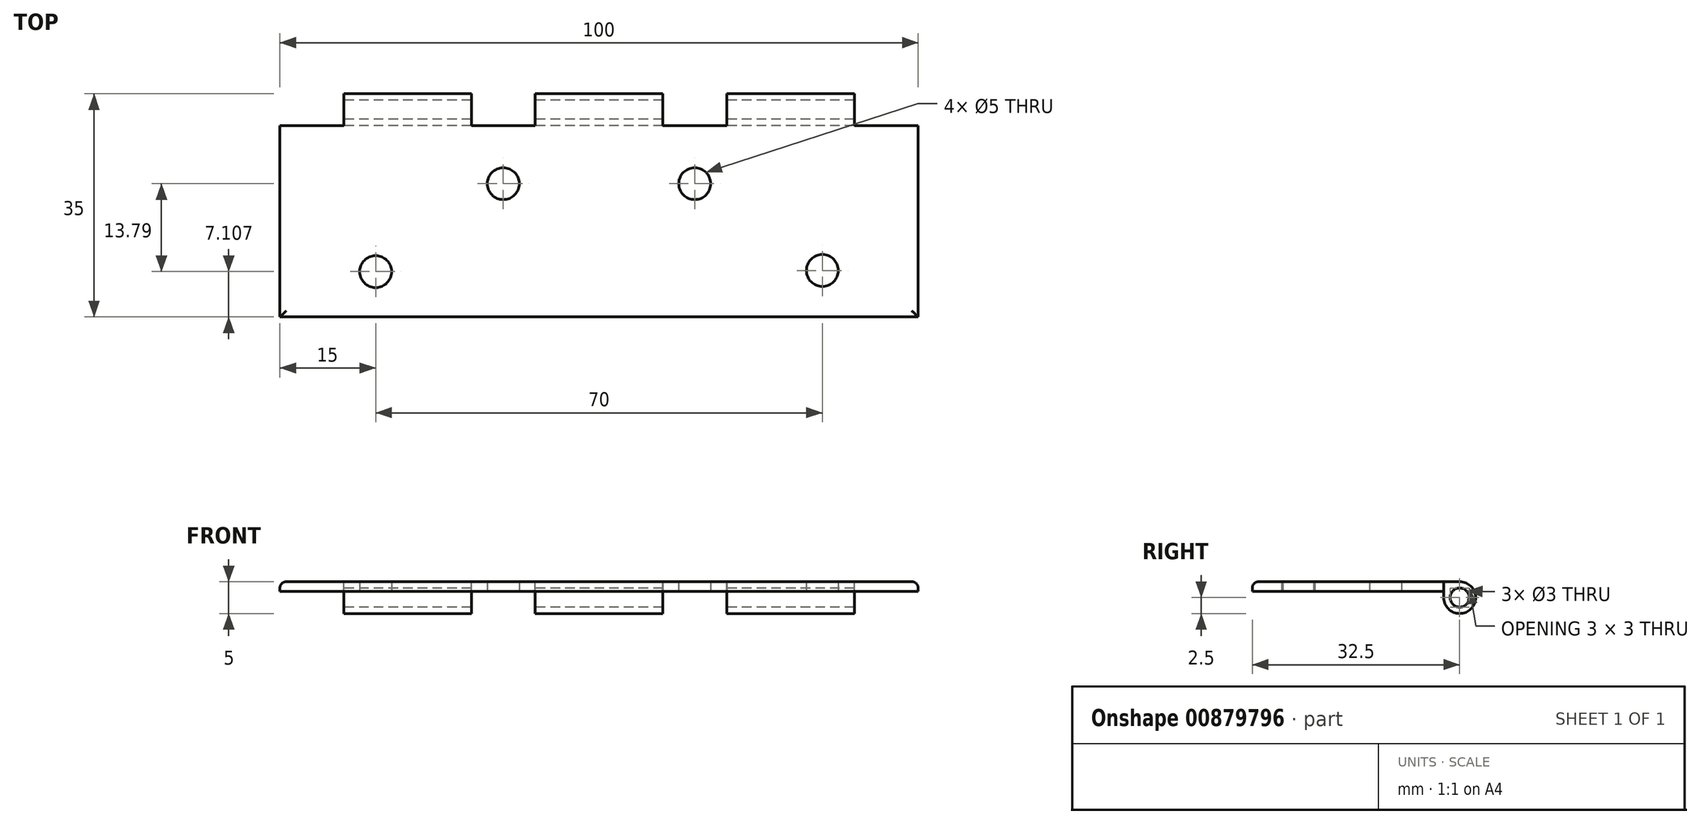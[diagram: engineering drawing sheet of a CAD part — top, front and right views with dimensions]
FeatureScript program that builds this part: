
annotation { "Feature Type Name" : "Feature", "Feature Type Description" : "" }
export const myFeature = defineFeature(function(context is Context, id is Id, definition is map)
    precondition{}
    {
        {
            var Q0;
            Q0=qCreatedBy(makeId("Top.planeOp"),FACE);
            var sketch = newSketch(context, id + "F0", { "sketchPlane" : qUnion([Q0])});
            skLineSegment(sketch, "E0.bottom", {"start": v(-50, 15) * mm, "end": v(50, 15) * mm});
            skLineSegment(sketch, "E0.top", {"start": v(-50, -15) * mm, "end": v(50, -15) * mm});
            skLineSegment(sketch, "E0.left", {"start": v(-50, 15) * mm, "end": v(-50, -15) * mm});
            skLineSegment(sketch, "E0.right", {"start": v(50, 15) * mm, "end": v(50, -15) * mm});
            skCircle(sketch, "E1", {"center": v(-35, -7.9) * mm, "radius": 2.5 * mm});
            skCircle(sketch, "E2", {"center": v(-15, 5.9) * mm, "radius": 2.5 * mm});
            skCircle(sketch, "E3", {"center": v(15, 5.9) * mm, "radius": 2.5 * mm});
            skCircle(sketch, "E4", {"center": v(35, -7.71) * mm, "radius": 2.5 * mm});
            skSolve(sketch);
        }
        {
            var Q0;
            Q0=makeQuery(id+"F0.imprint","IMPRINT",FACE,{"disambiguationData":[TD([[makeQuery(id+"F0.imprint","IMPRINT",EDGE,{"derivedFrom":sQuery(id+"F0.wireOp",EDGE,"E0.bottom")}),-1.0]])]});
            extrude(context, id + "F1", {"entities" : qUnion([Q0]), "depth" : 5 * mm, "offsetDistance" : 25 * mm});
        }
        {
            var Q0;
            Q0=makeQuery(id+"F1.opExtrude","SWEPT_FACE",FACE,{"disambiguationData":[OSD([sQuery(id+"F0.wireOp",EDGE,"E0.left")])]});
            var sketch = newSketch(context, id + "F2", { "sketchPlane" : qUnion([Q0])});
            skArc(sketch, "E5", {"start": v(-17.5, 5) * mm, "mid": v(-20, 2.5) * mm, "end": v(-17.5, 0) * mm});
            skLineSegment(sketch, "E6", {"start": v(-15, 5) * mm, "end": v(-17.5, 5) * mm});
            skLineSegment(sketch, "E7", {"start": v(-15, 0) * mm, "end": v(-17.5, 0) * mm});
            skCircle(sketch, "E8", {"center": v(-17.5, 2.5) * mm, "radius": 1.5 * mm});
            skSolve(sketch);
        }
        {
            var Q0;
            Q0=makeQuery(id+"F2.imprint","IMPRINT",FACE,{"disambiguationData":[TD([[makeQuery(id+"F2.imprint","IMPRINT",EDGE,{"derivedFrom":sQuery(id+"F2.wireOp",EDGE,"E5")}),1.0]])]});
            extrude(context, id + "F3", {"entities" : qUnion([Q0]), "operationType" : NewBodyOperationType.ADD, "oppositeDirection" : true, "depth" : 100 * mm, "offsetDistance" : 25 * mm});
        }
        {
            var Q0;
            Q0=makeQuery(id+"F3.boolean.opBoolean","MERGE",FACE,{"derivedFrom":[makeQuery(id+"F1.opExtrude","CAP_FACE",FACE,{"disambiguationData":[OSD([sQuery(id+"F0.wireOp",EDGE,"E0.bottom"),sQuery(id+"F0.wireOp",EDGE,"E0.top"),sQuery(id+"F0.wireOp",EDGE,"E0.left"),sQuery(id+"F0.wireOp",EDGE,"E0.right"),sQuery(id+"F0.wireOp",EDGE,"E1"),sQuery(id+"F0.wireOp",EDGE,"E2"),sQuery(id+"F0.wireOp",EDGE,"E3"),sQuery(id+"F0.wireOp",EDGE,"E4")])],"isStart":false}),makeQuery(id+"F3.opExtrude","SWEPT_FACE",FACE,{"disambiguationData":[OSD([sQuery(id+"F2.wireOp",EDGE,"E6")])]})]});
            var sketch = newSketch(context, id + "F4", { "sketchPlane" : qUnion([Q0])});
            skLineSegment(sketch, "E9", {"start": v(0, 0) * mm, "end": v(-50, 0) * mm, "construction": true});
            skLineSegment(sketch, "E10", {"start": v(-50, 15) * mm, "end": v(50, 15) * mm, "construction": true});
            skLineSegment(sketch, "E11.bottom", {"start": v(-50, 15) * mm, "end": v(-40, 15) * mm});
            skLineSegment(sketch, "E11.top", {"start": v(-50, 20) * mm, "end": v(-40, 20) * mm});
            skLineSegment(sketch, "E11.left", {"start": v(-50, 15) * mm, "end": v(-50, 20) * mm});
            skLineSegment(sketch, "E11.right", {"start": v(-40, 15) * mm, "end": v(-40, 20) * mm});
            skLineSegment(sketch, "E12.bottom", {"start": v(-20, 15) * mm, "end": v(-10, 15) * mm});
            skLineSegment(sketch, "E12.top", {"start": v(-20, 20) * mm, "end": v(-10, 20) * mm});
            skLineSegment(sketch, "E12.left", {"start": v(-20, 15) * mm, "end": v(-20, 20) * mm});
            skLineSegment(sketch, "E12.right", {"start": v(-10, 15) * mm, "end": v(-10, 20) * mm});
            skLineSegment(sketch, "E13.bottom", {"start": v(10, 20) * mm, "end": v(20, 20) * mm});
            skLineSegment(sketch, "E13.top", {"start": v(10, 15) * mm, "end": v(20, 15) * mm});
            skLineSegment(sketch, "E13.left", {"start": v(10, 20) * mm, "end": v(10, 15) * mm});
            skLineSegment(sketch, "E13.right", {"start": v(20, 20) * mm, "end": v(20, 15) * mm});
            skLineSegment(sketch, "E14.bottom", {"start": v(50, 15) * mm, "end": v(40, 15) * mm});
            skLineSegment(sketch, "E14.top", {"start": v(50, 20) * mm, "end": v(40, 20) * mm});
            skLineSegment(sketch, "E14.left", {"start": v(50, 15) * mm, "end": v(50, 20) * mm});
            skLineSegment(sketch, "E14.right", {"start": v(40, 15) * mm, "end": v(40, 20) * mm});
            skSolve(sketch);
        }
        {
            var Q0;
            {var subQ0=sQuery(id+"F4.wireOp",EDGE,"E11.top");Q0=makeQuery(id+"F4.imprint","IMPRINT",FACE,{"disambiguationData":[TD([[makeQuery(id+"F4.imprint","IMPRINT",EDGE,{"derivedFrom":subQ0}),-1.0]])]});}
            var Q1;
            {var subQ0=sQuery(id+"F4.wireOp",EDGE,"E11.bottom");Q1=makeQuery(id+"F4.imprint","IMPRINT",FACE,{"disambiguationData":[TD([[makeQuery(id+"F4.imprint","IMPRINT",EDGE,{"derivedFrom":subQ0}),1.0]])]});}
            var Q2;
            {var subQ0=sQuery(id+"F4.wireOp",EDGE,"E12.top");Q2=makeQuery(id+"F4.imprint","IMPRINT",FACE,{"disambiguationData":[TD([[makeQuery(id+"F4.imprint","IMPRINT",EDGE,{"derivedFrom":subQ0}),-1.0]])]});}
            var Q3;
            {var subQ0=sQuery(id+"F4.wireOp",EDGE,"E12.bottom");Q3=makeQuery(id+"F4.imprint","IMPRINT",FACE,{"disambiguationData":[TD([[makeQuery(id+"F4.imprint","IMPRINT",EDGE,{"derivedFrom":subQ0}),1.0]])]});}
            var Q4;
            {var subQ0=sQuery(id+"F4.wireOp",EDGE,"E13.bottom");Q4=makeQuery(id+"F4.imprint","IMPRINT",FACE,{"disambiguationData":[TD([[makeQuery(id+"F4.imprint","IMPRINT",EDGE,{"derivedFrom":subQ0}),-1.0]])]});}
            var Q5;
            {var subQ0=sQuery(id+"F4.wireOp",EDGE,"E13.top");Q5=makeQuery(id+"F4.imprint","IMPRINT",FACE,{"disambiguationData":[TD([[makeQuery(id+"F4.imprint","IMPRINT",EDGE,{"derivedFrom":subQ0}),1.0]])]});}
            var Q6;
            {var subQ0=sQuery(id+"F4.wireOp",EDGE,"E14.top");Q6=makeQuery(id+"F4.imprint","IMPRINT",FACE,{"disambiguationData":[TD([[makeQuery(id+"F4.imprint","IMPRINT",EDGE,{"derivedFrom":subQ0}),1.0]])]});}
            var Q7;
            {var subQ0=sQuery(id+"F4.wireOp",EDGE,"E14.bottom");Q7=makeQuery(id+"F4.imprint","IMPRINT",FACE,{"disambiguationData":[TD([[makeQuery(id+"F4.imprint","IMPRINT",EDGE,{"derivedFrom":subQ0}),-1.0]])]});}
            extrude(context, id + "F5", {"entities" : qUnion([Q0, Q1, Q2, Q3, Q4, Q5, Q6, Q7]), "operationType" : NewBodyOperationType.REMOVE, "oppositeDirection" : true, "depth" : 25 * mm, "offsetDistance" : 25 * mm});
        }
        {
            var Q0;
            Q0=makeQuery(id+"F3.boolean.opBoolean","MERGE",EDGE,{"derivedFrom":[makeQuery(id+"F1.opExtrude","CAP_EDGE",EDGE,{"disambiguationData":[OSD([sQuery(id+"F0.wireOp",EDGE,"E0.left")])],"isStart":false}),makeQuery(id+"F3.opExtrude","CAP_EDGE",EDGE,{"disambiguationData":[OSD([sQuery(id+"F2.wireOp",EDGE,"E6")])],"isStart":true})]});
            var Q1;
            Q1=makeQuery(id+"F3.boolean.opBoolean","MERGE",EDGE,{"derivedFrom":[makeQuery(id+"F1.opExtrude","CAP_EDGE",EDGE,{"disambiguationData":[OSD([sQuery(id+"F0.wireOp",EDGE,"E0.left")])],"isStart":true}),makeQuery(id+"F3.opExtrude","CAP_EDGE",EDGE,{"disambiguationData":[OSD([sQuery(id+"F2.wireOp",EDGE,"E7")])],"isStart":true})]});
            var Q2;
            Q2=makeQuery(id+"F1.opExtrude","CAP_EDGE",EDGE,{"disambiguationData":[OSD([sQuery(id+"F0.wireOp",EDGE,"E0.top")])],"isStart":true});
            var Q3;
            Q3=makeQuery(id+"F1.opExtrude","CAP_EDGE",EDGE,{"disambiguationData":[OSD([sQuery(id+"F0.wireOp",EDGE,"E0.top")])],"isStart":false});
            var Q4;
            Q4=makeQuery(id+"F3.boolean.opBoolean","MERGE",EDGE,{"derivedFrom":[makeQuery(id+"F1.opExtrude","CAP_EDGE",EDGE,{"disambiguationData":[OSD([sQuery(id+"F0.wireOp",EDGE,"E0.right")])],"isStart":false}),makeQuery(id+"F3.opExtrude","CAP_EDGE",EDGE,{"disambiguationData":[OSD([sQuery(id+"F2.wireOp",EDGE,"E6")])],"isStart":false})]});
            var Q5;
            Q5=makeQuery(id+"F3.boolean.opBoolean","MERGE",EDGE,{"derivedFrom":[makeQuery(id+"F1.opExtrude","CAP_EDGE",EDGE,{"disambiguationData":[OSD([sQuery(id+"F0.wireOp",EDGE,"E0.right")])],"isStart":true}),makeQuery(id+"F3.opExtrude","CAP_EDGE",EDGE,{"disambiguationData":[OSD([sQuery(id+"F2.wireOp",EDGE,"E7")])],"isStart":false})]});
            fillet(context, id + "F6", {"entities" : qUnion([Q0, Q1, Q2, Q3, Q4, Q5]), "radius" : 1 * mm, "tangentPropagation" : true, "allowEdgeOverflow" : false});
        }
        {
            var Q0;
            {var subQ0=sQuery(id+"F0.wireOp",EDGE,"E0.left");Q0=makeQuery(id+"F3.boolean.opBoolean","MERGE",FACE,{"derivedFrom":[makeQuery(id+"F1.opExtrude","SWEPT_FACE",FACE,{"disambiguationData":[OSD([subQ0])]}),makeQuery(id+"F3.opExtrude","CAP_FACE",FACE,{"disambiguationData":[OSD([sQuery(id+"F0.wireOp",EDGE,"E0.bottom"),subQ0,sQuery(id+"F2.wireOp",EDGE,"E5"),sQuery(id+"F2.wireOp",EDGE,"E6"),sQuery(id+"F2.wireOp",EDGE,"E7"),sQuery(id+"F2.wireOp",EDGE,"E8")])],"isStart":true})]});}
            var sketch = newSketch(context, id + "F7", { "sketchPlane" : qUnion([Q0])});
            skPoint(sketch, "E15.centerSnap0", {"position": v(-15, 2.5) * mm});
            skCircle(sketch, "E16", {"center": v(-17.5, 2.5) * mm, "radius": 2.5 * mm});
            skLineSegment(sketch, "E17.bottom", {"start": v(-17.5, 5) * mm, "end": v(15, 5) * mm});
            skLineSegment(sketch, "E17.top", {"start": v(-15.2, 3.5) * mm, "end": v(15, 3.5) * mm});
            skLineSegment(sketch, "E17.right", {"start": v(15, 5) * mm, "end": v(15, 3.5) * mm});
            skLineSegment(sketch, "E18.top", {"start": v(-17.5, 0) * mm, "end": v(15, 0) * mm});
            skLineSegment(sketch, "E18.right", {"start": v(15, 3.5) * mm, "end": v(15, 0) * mm});
            skPoint(sketch, "E19.orphan", {"position": v(-17.5, 3.5) * mm});
            skSolve(sketch);
        }
        {
            var Q0;
            {var subQ6=sQuery(id+"F7.wireOp",EDGE,"E18.right");var subQ7=sQuery(id+"F7.wireOp",EDGE,"E17.top");var subQ8=makeQuery(id+"F7.imprint","INTERSECT",VERTEX,{"derivedFrom":[sQuery(id+"F7.wireOp",EDGE,"E17.right"),subQ7,subQ6]});Q0=makeQuery(id+"F7.imprint","IMPRINT",FACE,{"disambiguationData":[TD([[makeQuery(id+"F7.imprint","IMPRINT",EDGE,{"disambiguationData":[TD([[subQ8,1.0]])],"derivedFrom":subQ7}),-1.0]])]});}
            var Q1;
            {var subQ5=sQuery(id+"F7.wireOp",EDGE,"E18.top");Q1=makeQuery(id+"F7.imprint","IMPRINT",FACE,{"disambiguationData":[TD([[makeQuery(id+"F7.imprint","IMPRINT",EDGE,{"derivedFrom":subQ5}),1.0]])]});}
            extrude(context, id + "F8", {"entities" : qUnion([Q0, Q1]), "operationType" : NewBodyOperationType.REMOVE, "endBound" : BoundingType.THROUGH_ALL, "oppositeDirection" : true, "depth" : 25 * mm, "offsetDistance" : 25 * mm});
        }
    });
